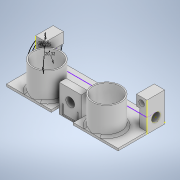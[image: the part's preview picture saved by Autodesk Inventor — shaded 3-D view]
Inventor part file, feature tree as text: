
AUTODESK INVENTOR PART (.ipt)
format: ipt  version: 2020 (Build 240168000, 168)  size: 379,392 bytes
history: native  units: mm
features: sketch x27, extrude x18, fillet x2
ambient origin geometry x8: Origin, YZ Plane, XZ Plane, XY Plane, X Axis, Y Axis, Z Axis, Center Point
bodies: Solid1 (feature_tree)
feature tree (47):
  sketch  "Sketch1"  dims[d3=25.4mm d4=25.4mm]
  extrude  "Extrusion1"  Depth=25.4mm
  extrude  "Extrusion2"  Depth=10.0mm TaperAngle=0.0deg
  extrude  "Extrusion3"  Depth=15.0mm
  sketch  "Sketch6"  dims[d14=14.85mm d15=0.0mm d16=20.32mm]
  extrude  "Extrusion4"  Depth=25.4mm TaperAngle=0.0deg
  sketch  "Sketch8"  dims[d19=3.25mm d20=150.0mm d21=10.0mm d22=0.0mm d23=0.0mm]
  extrude  "Extrusion5"  Depth=20.32mm
  extrude  "Extrusion6"  Depth=2.0mm
  sketch  "Sketch11"  dims[d29=25.4mm d30=0.0mm d31=18.0mm]
  extrude  "Extrusion7"  Depth=150.0mm TaperAngle=0.0deg
  extrude  "Extrusion8"  Depth=15.0mm
  extrude  "Extrusion9"  Depth=8.0mm
  sketch  "Sketch14"  dims[d39=31.75mm d40=20.0mm d41=0.0mm]
  sketch  "Sketch15"  dims[d42=25.0mm d43=10.0mm d44=0.0mm]
  sketch  "Sketch16"  dims[d45=31.75mm d46=10.0mm d47=0.0mm d48=12.7mm]
  extrude  "Extrusion10"  Depth=18.0mm
  extrude  "Extrusion11"  Depth=7.4mm
  sketch  "Sketch19"  dims[d60=1.5875mm d61=6.35mm d62=50.8mm]
  sketch  "Sketch20"  dims[d63=8.0mm]
  extrude  "Extrusion12"  Depth=14.9mm TaperAngle=0.0deg
  extrude  "Extrusion13"  Depth=20.0mm TaperAngle=0.0deg
  sketch  "Sketch23"  dims[d68=9.0mm]
  sketch  "Sketch24"  dims[d70=41.5mm]
  extrude  "Extrusion14"  Depth=10.0mm TaperAngle=0.0deg
  extrude  "Extrusion15"  Depth=10.0mm TaperAngle=0.0deg
  fillet  "Fillet1"  Radius=12.7mm
  sketch  "Sketch26"  dims[d74=41.5mm]
  extrude  "Extrusion16"  Depth=21.0mm
  extrude  "Extrusion17"  Depth=1.5875mm
  extrude  "Extrusion18"  Depth=6.35mm
  fillet  "Fillet2"  Radius=50.8mm
  sketch  "Sketch2"  dims[d5=12.7mm d6=10.0mm d7=0.0mm]
  sketch  "Sketch3"  dims[d8=15.0mm d9=15.0mm]
  sketch  "Sketch4"  dims[d10=8.0mm d11=25.4mm d12=0.0mm]
  sketch  "Sketch7"  dims[d17=41.275mm d18=2.0mm]
  sketch  "Sketch9"  dims[d24=10.0mm d25=0.0mm d26=15.0mm]
  sketch  "Sketch10"  dims[d27=15.0mm d28=8.0mm]
  sketch  "Sketch12"  dims[d32=25.4mm d33=0.0mm d34=7.4mm]
  sketch  "Sketch13"  dims[d35=14.9mm d36=0.0mm d37=14.9mm d38=0.0mm]
  sketch  "Sketch17"  dims[d49=10.0mm d50=0.0mm d51=21.0mm]
  sketch  "Sketch18"  dims[d58=1.5875mm d59=1.5875mm]
  sketch  "Sketch21"  dims[d64=20.0mm d65=0.0mm]
  sketch  "Sketch22"  dims[d66=15.0mm d67=0.0mm]
  sketch  "Sketch25"  dims[d71=0.5mm d72=0.0mm]
  sketch  "Sketch27"  dims[d75=3.25mm d76=0.0mm]
  sketch  "Sketch28"  dims[d78=38.0mm d79=39.0mm d80=0.0mm d81=3.0mm d73=0.5mm d82=0.872665mm]
